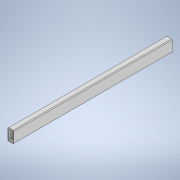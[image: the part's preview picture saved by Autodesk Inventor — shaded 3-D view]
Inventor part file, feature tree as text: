
AUTODESK INVENTOR PART (.ipt)
format: ipt  version: 2020 (Build 240168000, 168)  size: 126,464 bytes
history: native  units: in
note: dims shown in document units (in); Inventor stores cm internally (conversion verified against a paired STEP export)
features: extrude x1, sketch x1
ambient origin geometry x8: Origin, YZ Plane, XZ Plane, XY Plane, X Axis, Y Axis, Z Axis, Center Point
bodies: Solid1 (feature_tree)
feature tree (2):
  extrude  "Extrusion1"  Depth=1.0in
  sketch  "Sketch1"  dims[d0=2.0in d1=1.0in d2=0.125in d3=0.125in d4=0.125in d5=0.125in d6=0.125in d7=0.125in d8=0.125in d9=0.125in d10=0.125in d11=27.0in d12=0.0in]
